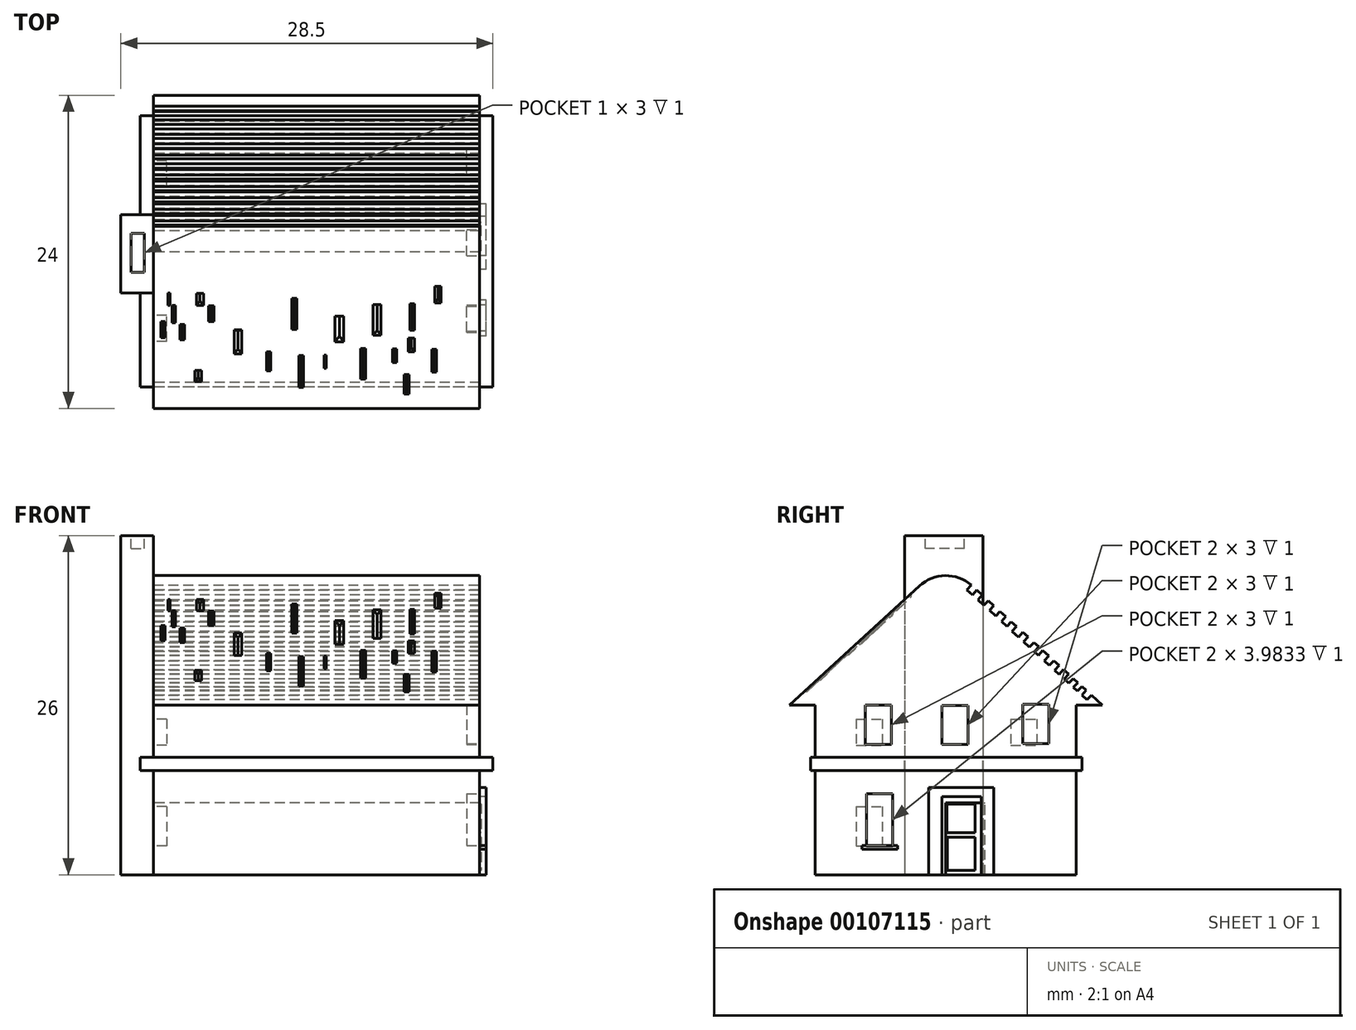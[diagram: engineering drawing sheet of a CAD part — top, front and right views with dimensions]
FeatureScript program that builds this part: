
annotation { "Feature Type Name" : "Feature", "Feature Type Description" : "" }
export const myFeature = defineFeature(function(context is Context, id is Id, definition is map)
    precondition{}
    {
        {
            var Q0;
            Q0=qCreatedBy(makeId("Right.planeOp"),FACE);
            var sketch = newSketch(context, id + "F0", { "sketchPlane" : qUnion([Q0])});
            skLineSegment(sketch, "E0.bottom", {"start": v(0, 0) * mm, "end": v(20, 0) * mm});
            skLineSegment(sketch, "E0.top", {"start": v(0, 13) * mm, "end": v(20, 13) * mm});
            skLineSegment(sketch, "E0.left", {"start": v(0, 0) * mm, "end": v(0, 13) * mm});
            skLineSegment(sketch, "E0.right", {"start": v(20, 0) * mm, "end": v(20, 13) * mm});
            skLineSegment(sketch, "E1", {"start": v(10, 13) * mm, "end": v(10, 24) * mm, "construction": true});
            skLineSegment(sketch, "E2", {"start": v(0, 13) * mm, "end": v(-2, 13) * mm});
            skLineSegment(sketch, "E3", {"start": v(20, 13) * mm, "end": v(22, 13) * mm});
            skLineSegment(sketch, "E4", {"start": v(-2, 13) * mm, "end": v(10, 24) * mm});
            skLineSegment(sketch, "E5", {"start": v(22, 13) * mm, "end": v(10, 24) * mm});
            skLineSegment(sketch, "E6.bottom", {"start": v(10, 0) * mm, "end": v(13, 0) * mm});
            skLineSegment(sketch, "E6.top", {"start": v(10, 5.5) * mm, "end": v(13, 5.5) * mm});
            skLineSegment(sketch, "E6.left", {"start": v(10, 0) * mm, "end": v(10, 5.5) * mm});
            skLineSegment(sketch, "E6.right", {"start": v(13, 0) * mm, "end": v(13, 5.5) * mm});
            skLineSegment(sketch, "E7.bottom", {"start": v(3.14, 5.21) * mm, "end": v(5.14, 5.21) * mm});
            skLineSegment(sketch, "E7.top", {"start": v(3.14, 2.21) * mm, "end": v(5.14, 2.21) * mm});
            skLineSegment(sketch, "E7.left", {"start": v(3.14, 5.21) * mm, "end": v(3.14, 2.21) * mm});
            skLineSegment(sketch, "E7.right", {"start": v(5.14, 5.21) * mm, "end": v(5.14, 2.21) * mm});
            skLineSegment(sketch, "E8.bottom", {"start": v(3.14, 11.94) * mm, "end": v(5.14, 11.94) * mm});
            skLineSegment(sketch, "E8.top", {"start": v(3.14, 9.94) * mm, "end": v(5.14, 9.94) * mm});
            skLineSegment(sketch, "E8.left", {"start": v(3.14, 11.94) * mm, "end": v(3.14, 9.94) * mm});
            skLineSegment(sketch, "E8.right", {"start": v(5.14, 11.94) * mm, "end": v(5.14, 9.94) * mm});
            skLineSegment(sketch, "E9.bottom", {"start": v(8.85, 11.94) * mm, "end": v(10.85, 11.94) * mm});
            skLineSegment(sketch, "E9.top", {"start": v(8.85, 9.94) * mm, "end": v(10.85, 9.94) * mm});
            skLineSegment(sketch, "E9.left", {"start": v(8.85, 11.94) * mm, "end": v(8.85, 9.94) * mm});
            skLineSegment(sketch, "E9.right", {"start": v(10.85, 11.94) * mm, "end": v(10.85, 9.94) * mm});
            skLineSegment(sketch, "E10.bottom", {"start": v(14.97, 11.94) * mm, "end": v(16.97, 11.94) * mm});
            skLineSegment(sketch, "E10.top", {"start": v(14.97, 9.94) * mm, "end": v(16.97, 9.94) * mm});
            skLineSegment(sketch, "E10.left", {"start": v(14.97, 11.94) * mm, "end": v(14.97, 9.94) * mm});
            skLineSegment(sketch, "E10.right", {"start": v(16.97, 11.94) * mm, "end": v(16.97, 9.94) * mm});
            skSolve(sketch);
        }
        {
            var Q0;
            Q0=makeQuery(id+"F0.imprint","IMPRINT",FACE,{"disambiguationData":[TD([[makeQuery(id+"F0.imprint","IMPRINT",EDGE,{"derivedFrom":sQuery(id+"F0.wireOp",EDGE,"E0.top")}),1.0]])]});
            var Q1;
            Q1=makeQuery(id+"F0.imprint","IMPRINT",FACE,{"disambiguationData":[TD([[makeQuery(id+"F0.imprint","IMPRINT",EDGE,{"derivedFrom":sQuery(id+"F0.wireOp",EDGE,"E8.bottom")}),-1.0]])]});
            var Q2;
            Q2=makeQuery(id+"F0.imprint","IMPRINT",FACE,{"disambiguationData":[TD([[makeQuery(id+"F0.imprint","IMPRINT",EDGE,{"derivedFrom":sQuery(id+"F0.wireOp",EDGE,"E9.bottom")}),-1.0]])]});
            var Q3;
            Q3=makeQuery(id+"F0.imprint","IMPRINT",FACE,{"disambiguationData":[TD([[makeQuery(id+"F0.imprint","IMPRINT",EDGE,{"derivedFrom":sQuery(id+"F0.wireOp",EDGE,"E10.bottom")}),-1.0]])]});
            var Q4;
            Q4=makeQuery(id+"F0.imprint","IMPRINT",FACE,{"disambiguationData":[TD([[makeQuery(id+"F0.imprint","IMPRINT",EDGE,{"derivedFrom":sQuery(id+"F0.wireOp",EDGE,"E6.bottom")}),1.0]])]});
            var Q5;
            Q5=makeQuery(id+"F0.imprint","IMPRINT",FACE,{"disambiguationData":[TD([[makeQuery(id+"F0.imprint","IMPRINT",EDGE,{"derivedFrom":sQuery(id+"F0.wireOp",EDGE,"E7.bottom")}),-1.0]])]});
            var Q6;
            Q6=makeQuery(id+"F0.imprint","IMPRINT",FACE,{"disambiguationData":[TD([[makeQuery(id+"F0.imprint","IMPRINT",EDGE,{"derivedFrom":sQuery(id+"F0.wireOp",EDGE,"E0.top")}),-1.0]])]});
            extrude(context, id + "F1", {"entities" : qUnion([Q0, Q1, Q2, Q3, Q4, Q5, Q6]), "depth" : 25 * mm});
        }
        {
            var Q0;
            Q0=makeQuery(id+"F0.imprint","IMPRINT",FACE,{"disambiguationData":[TD([[makeQuery(id+"F0.imprint","IMPRINT",EDGE,{"derivedFrom":sQuery(id+"F0.wireOp",EDGE,"E10.bottom")}),-1.0]])]});
            var Q1;
            Q1=makeQuery(id+"F0.imprint","IMPRINT",FACE,{"disambiguationData":[TD([[makeQuery(id+"F0.imprint","IMPRINT",EDGE,{"derivedFrom":sQuery(id+"F0.wireOp",EDGE,"E8.bottom")}),-1.0]])]});
            var Q2;
            Q2=makeQuery(id+"F0.imprint","IMPRINT",FACE,{"disambiguationData":[TD([[makeQuery(id+"F0.imprint","IMPRINT",EDGE,{"derivedFrom":sQuery(id+"F0.wireOp",EDGE,"E7.bottom")}),-1.0]])]});
            extrude(context, id + "F2", {"entities" : qUnion([Q0, Q1, Q2]), "operationType" : NewBodyOperationType.REMOVE, "depth" : 1 * mm});
        }
        {
            var Q0;
            Q0=makeQuery(id+"F1.opExtrude","CAP_FACE",FACE,{"disambiguationData":[OSD([sQuery(id+"F0.wireOp",EDGE,"E0.bottom"),sQuery(id+"F0.wireOp",EDGE,"E0.left"),sQuery(id+"F0.wireOp",EDGE,"E0.right"),sQuery(id+"F0.wireOp",EDGE,"E2"),sQuery(id+"F0.wireOp",EDGE,"E3"),sQuery(id+"F0.wireOp",EDGE,"E4"),sQuery(id+"F0.wireOp",EDGE,"E5"),sQuery(id+"F0.wireOp",EDGE,"E6.bottom")])],"isStart":false});
            cPlane(context, id + "F3", {"entities" : qUnion([Q0]), "cplaneType" : CPlaneType.OFFSET, "offset" : 0 * mm, "width" : 150 * mm, "height" : 150 * mm});
        }
        {
            var Q0;
            Q0=qCreatedBy(id+"F3.planeOp",FACE);
            var sketch = newSketch(context, id + "F4", { "sketchPlane" : qUnion([Q0])});
            skLineSegment(sketch, "E11.bottom", {"start": v(3.83, 13) * mm, "end": v(5.83, 13) * mm});
            skLineSegment(sketch, "E11.top", {"start": v(3.83, 10) * mm, "end": v(5.83, 10) * mm});
            skLineSegment(sketch, "E11.left", {"start": v(3.83, 13) * mm, "end": v(3.83, 10) * mm});
            skLineSegment(sketch, "E11.right", {"start": v(5.83, 13) * mm, "end": v(5.83, 10) * mm});
            skLineSegment(sketch, "E12.bottom", {"start": v(9.7, 12.98) * mm, "end": v(11.7, 12.98) * mm});
            skLineSegment(sketch, "E12.top", {"start": v(9.7, 9.98) * mm, "end": v(11.7, 9.98) * mm});
            skLineSegment(sketch, "E12.left", {"start": v(9.7, 12.98) * mm, "end": v(9.7, 9.98) * mm});
            skLineSegment(sketch, "E12.right", {"start": v(11.7, 12.98) * mm, "end": v(11.7, 9.98) * mm});
            skLineSegment(sketch, "E13.bottom", {"start": v(15.88, 13.05) * mm, "end": v(17.88, 13.05) * mm});
            skLineSegment(sketch, "E13.top", {"start": v(15.88, 10.05) * mm, "end": v(17.88, 10.05) * mm});
            skLineSegment(sketch, "E13.left", {"start": v(15.88, 13.05) * mm, "end": v(15.88, 10.05) * mm});
            skLineSegment(sketch, "E13.right", {"start": v(17.88, 13.05) * mm, "end": v(17.88, 10.05) * mm});
            skLineSegment(sketch, "E14.bottom", {"start": v(3.92, 6.22) * mm, "end": v(5.92, 6.22) * mm});
            skLineSegment(sketch, "E14.top", {"start": v(3.92, 2.22) * mm, "end": v(5.92, 2.22) * mm});
            skLineSegment(sketch, "E14.left", {"start": v(3.92, 6.22) * mm, "end": v(3.92, 2.22) * mm});
            skLineSegment(sketch, "E14.right", {"start": v(5.92, 6.22) * mm, "end": v(5.92, 2.22) * mm});
            skLineSegment(sketch, "E15.bottom", {"start": v(9.72, 6) * mm, "end": v(12.72, 6) * mm});
            skLineSegment(sketch, "E15.top", {"start": v(9.72, 0) * mm, "end": v(12.72, 0) * mm});
            skLineSegment(sketch, "E15.left", {"start": v(9.72, 6) * mm, "end": v(9.72, 0) * mm});
            skLineSegment(sketch, "E15.right", {"start": v(12.72, 6) * mm, "end": v(12.72, 0) * mm});
            skLineSegment(sketch, "E16.bottom", {"start": v(8.67, 6.7) * mm, "end": v(13.67, 6.7) * mm});
            skLineSegment(sketch, "E16.top", {"start": v(8.67, 0) * mm, "end": v(13.67, 0) * mm});
            skLineSegment(sketch, "E16.left", {"start": v(8.67, 6.7) * mm, "end": v(8.67, 0) * mm});
            skLineSegment(sketch, "E16.right", {"start": v(13.67, 6.7) * mm, "end": v(13.67, 0) * mm});
            skLineSegment(sketch, "E17.bottom", {"start": v(10.09, 5.42) * mm, "end": v(12.24, 5.42) * mm});
            skLineSegment(sketch, "E17.top", {"start": v(10.09, 3.23) * mm, "end": v(12.24, 3.23) * mm});
            skLineSegment(sketch, "E17.left", {"start": v(10.09, 5.42) * mm, "end": v(10.09, 3.23) * mm});
            skLineSegment(sketch, "E17.right", {"start": v(12.24, 5.42) * mm, "end": v(12.24, 3.23) * mm});
            skLineSegment(sketch, "E18.bottom", {"start": v(10.13, 2.87) * mm, "end": v(12.24, 2.87) * mm});
            skLineSegment(sketch, "E18.top", {"start": v(10.13, 0.32) * mm, "end": v(12.24, 0.32) * mm});
            skLineSegment(sketch, "E18.left", {"start": v(10.13, 2.87) * mm, "end": v(10.13, 0.32) * mm});
            skLineSegment(sketch, "E18.right", {"start": v(12.24, 2.87) * mm, "end": v(12.24, 0.32) * mm});
            skLineSegment(sketch, "E19.bottom", {"start": v(3.56, 2.23) * mm, "end": v(6.3, 2.23) * mm});
            skLineSegment(sketch, "E19.top", {"start": v(3.56, 1.94) * mm, "end": v(6.3, 1.94) * mm});
            skLineSegment(sketch, "E19.left", {"start": v(3.56, 2.23) * mm, "end": v(3.56, 1.94) * mm});
            skLineSegment(sketch, "E19.right", {"start": v(6.3, 2.23) * mm, "end": v(6.3, 1.94) * mm});
            skLineSegment(sketch, "E20", {"start": v(0, 9) * mm, "end": v(20.43, 9) * mm});
            skLineSegment(sketch, "E21", {"start": v(20.43, 9) * mm, "end": v(20.43, 8) * mm});
            skLineSegment(sketch, "E22", {"start": v(20.43, 8) * mm, "end": v(-0.36, 8) * mm});
            skLineSegment(sketch, "E23", {"start": v(-0.36, 8) * mm, "end": v(-0.36, 9) * mm});
            skLineSegment(sketch, "E24", {"start": v(-0.36, 9) * mm, "end": v(0, 9) * mm});
            skSolve(sketch);
        }
        {
            var Q0;
            {var subQ5=sQuery(id+"F4.wireOp",EDGE,"E14.top");Q0=makeQuery(id+"F4.imprint","IMPRINT",FACE,{"disambiguationData":[TD([[makeQuery(id+"F4.imprint","IMPRINT",EDGE,{"derivedFrom":subQ5}),-1.0]])]});}
            var Q1;
            Q1=makeQuery(id+"F4.imprint","IMPRINT",FACE,{"disambiguationData":[TD([[makeQuery(id+"F4.imprint","IMPRINT",EDGE,{"derivedFrom":sQuery(id+"F4.wireOp",EDGE,"E15.bottom")}),1.0]])]});
            extrude(context, id + "F5", {"entities" : qUnion([Q0, Q1]), "operationType" : NewBodyOperationType.ADD, "depth" : .5 * mm});
        }
        {
            var Q0;
            {var subQ0=sQuery(id+"F4.wireOp",EDGE,"E14.bottom");Q0=makeQuery(id+"F4.imprint","IMPRINT",FACE,{"disambiguationData":[TD([[makeQuery(id+"F4.imprint","IMPRINT",EDGE,{"derivedFrom":subQ0}),-1.0]])]});}
            var Q1;
            Q1=makeQuery(id+"F4.imprint","IMPRINT",FACE,{"disambiguationData":[TD([[makeQuery(id+"F4.imprint","IMPRINT",EDGE,{"derivedFrom":sQuery(id+"F4.wireOp",EDGE,"E11.bottom")}),-1.0]])]});
            var Q2;
            Q2=makeQuery(id+"F4.imprint","IMPRINT",FACE,{"disambiguationData":[TD([[makeQuery(id+"F4.imprint","IMPRINT",EDGE,{"derivedFrom":sQuery(id+"F4.wireOp",EDGE,"E12.bottom")}),-1.0]])]});
            var Q3;
            Q3=makeQuery(id+"F4.imprint","IMPRINT",FACE,{"disambiguationData":[TD([[makeQuery(id+"F4.imprint","IMPRINT",EDGE,{"derivedFrom":sQuery(id+"F4.wireOp",EDGE,"E13.bottom")}),-1.0]])]});
            extrude(context, id + "F6", {"entities" : qUnion([Q0, Q1, Q2, Q3]), "operationType" : NewBodyOperationType.REMOVE, "oppositeDirection" : true, "depth" : 1 * mm});
        }
        {
            var Q0;
            Q0=makeQuery(id+"F4.imprint","IMPRINT",FACE,{"disambiguationData":[TD([[makeQuery(id+"F4.imprint","IMPRINT",EDGE,{"derivedFrom":sQuery(id+"F4.wireOp",EDGE,"E17.bottom")}),-1.0]])]});
            var Q1;
            Q1=makeQuery(id+"F4.imprint","IMPRINT",FACE,{"disambiguationData":[TD([[makeQuery(id+"F4.imprint","IMPRINT",EDGE,{"derivedFrom":sQuery(id+"F4.wireOp",EDGE,"E18.bottom")}),-1.0]])]});
            extrude(context, id + "F7", {"entities" : qUnion([Q0, Q1]), "operationType" : NewBodyOperationType.ADD, "depth" : .1 * mm});
        }
        {
            var Q0;
            Q0=qCreatedBy(makeId("Top.planeOp"),FACE);
            var sketch = newSketch(context, id + "F8", { "sketchPlane" : qUnion([Q0])});
            skLineSegment(sketch, "E25.bottom", {"start": v(0, 12.85) * mm, "end": v(-2.5, 12.85) * mm});
            skLineSegment(sketch, "E25.top", {"start": v(0, 6.85) * mm, "end": v(-2.5, 6.85) * mm});
            skLineSegment(sketch, "E25.left", {"start": v(0, 12.85) * mm, "end": v(0, 6.85) * mm});
            skLineSegment(sketch, "E25.right", {"start": v(-2.5, 12.85) * mm, "end": v(-2.5, 6.85) * mm});
            skSolve(sketch);
        }
        {
            var Q0;
            Q0=makeQuery(id+"F8.imprint","IMPRINT",FACE,{"disambiguationData":[TD([[makeQuery(id+"F8.imprint","IMPRINT",EDGE,{"derivedFrom":sQuery(id+"F8.wireOp",EDGE,"E25.bottom")}),1.0]])]});
            extrude(context, id + "F9", {"entities" : qUnion([Q0]), "operationType" : NewBodyOperationType.ADD, "depth" : 26 * mm});
        }
        {
            var Q0;
            Q0=makeQuery(id+"F9.opExtrude","CAP_FACE",FACE,{"disambiguationData":[OSD([sQuery(id+"F8.wireOp",EDGE,"E25.bottom"),sQuery(id+"F8.wireOp",EDGE,"E25.top"),sQuery(id+"F8.wireOp",EDGE,"E25.left"),sQuery(id+"F8.wireOp",EDGE,"E25.right")])],"isStart":false});
            cPlane(context, id + "F10", {"entities" : qUnion([Q0]), "cplaneType" : CPlaneType.OFFSET, "offset" : 0 * mm, "width" : 150 * mm, "height" : 150 * mm});
        }
        {
            var Q0;
            Q0=qCreatedBy(id+"F10.planeOp",FACE);
            var sketch = newSketch(context, id + "F11", { "sketchPlane" : qUnion([Q0])});
            skLineSegment(sketch, "E26.bottom", {"start": v(-1.7, 11.43) * mm, "end": v(-0.7, 11.43) * mm});
            skLineSegment(sketch, "E26.top", {"start": v(-1.7, 8.43) * mm, "end": v(-0.7, 8.43) * mm});
            skLineSegment(sketch, "E26.left", {"start": v(-1.7, 11.43) * mm, "end": v(-1.7, 8.43) * mm});
            skLineSegment(sketch, "E26.right", {"start": v(-0.7, 11.43) * mm, "end": v(-0.7, 8.43) * mm});
            skSolve(sketch);
        }
        {
            var Q0;
            Q0 = qSketchRegion(id + "F11", true);
            extrude(context, id + "F12", {"entities" : qUnion([Q0]), "operationType" : NewBodyOperationType.REMOVE, "oppositeDirection" : true, "depth" : 1 * mm});
        }
        {
            var Q0;
            Q0=makeQuery(id+"F1.opExtrude","SWEPT_EDGE",EDGE,{"disambiguationData":[OSD([sQuery(id+"F0.wireOp",EDGE,"E4"),sQuery(id+"F0.wireOp",EDGE,"E5")])]});
            fillet(context, id + "F13", {"entities" : qUnion([Q0]), "radius" : 3 * mm, "tangentPropagation" : true, "allowEdgeOverflow" : false});
        }
        {
            var Q0;
            Q0=makeQuery(id+"F4.imprint","IMPRINT",FACE,{"disambiguationData":[TD([[makeQuery(id+"F4.imprint","IMPRINT",EDGE,{"derivedFrom":sQuery(id+"F4.wireOp",EDGE,"E20")}),-1.0]])]});
            extrude(context, id + "F14", {"entities" : qUnion([Q0]), "operationType" : NewBodyOperationType.ADD, "depth" : 1 * mm, "hasSecondDirection" : true, "secondDirectionOppositeDirection" : true, "secondDirectionDepth" : 26 * mm});
        }
        {
            var Q0;
            Q0=makeQuery(id+"F1.opExtrude","SWEPT_FACE",FACE,{"disambiguationData":[OSD([sQuery(id+"F0.wireOp",EDGE,"E4")])]});
            var sketch = newSketch(context, id + "F15", { "sketchPlane" : qUnion([Q0])});
            skLineSegment(sketch, "E27.bottom", {"start": v(1.1, 19.31) * mm, "end": v(1.27, 19.31) * mm});
            skLineSegment(sketch, "E27.left", {"start": v(1.1, 19.31) * mm, "end": v(1.1, 18.01) * mm});
            skLineSegment(sketch, "E28.bottom", {"start": v(1.42, 18.01) * mm, "end": v(1.68, 18.01) * mm});
            skLineSegment(sketch, "E28.top", {"start": v(1.42, 16.2) * mm, "end": v(1.68, 16.2) * mm});
            skLineSegment(sketch, "E28.left", {"start": v(1.42, 18.01) * mm, "end": v(1.42, 16.2) * mm});
            skLineSegment(sketch, "E28.right", {"start": v(1.68, 18.01) * mm, "end": v(1.68, 16.2) * mm});
            skLineSegment(sketch, "E29.bottom", {"start": v(2.04, 16.05) * mm, "end": v(2.39, 16.05) * mm});
            skLineSegment(sketch, "E29.top", {"start": v(2.04, 14.43) * mm, "end": v(2.39, 14.43) * mm});
            skLineSegment(sketch, "E29.left", {"start": v(2.04, 16.05) * mm, "end": v(2.04, 14.43) * mm});
            skLineSegment(sketch, "E29.right", {"start": v(2.39, 16.05) * mm, "end": v(2.39, 14.43) * mm});
            skLineSegment(sketch, "E30.bottom", {"start": v(0.56, 16.32) * mm, "end": v(0.87, 16.32) * mm});
            skLineSegment(sketch, "E30.top", {"start": v(0.56, 14.66) * mm, "end": v(0.87, 14.66) * mm});
            skLineSegment(sketch, "E30.left", {"start": v(0.56, 16.32) * mm, "end": v(0.56, 14.66) * mm});
            skLineSegment(sketch, "E30.right", {"start": v(0.87, 16.32) * mm, "end": v(0.87, 14.66) * mm});
            skLineSegment(sketch, "E31.bottom", {"start": v(4.23, 17.97) * mm, "end": v(4.63, 17.97) * mm});
            skLineSegment(sketch, "E31.top", {"start": v(4.23, 16.36) * mm, "end": v(4.63, 16.36) * mm});
            skLineSegment(sketch, "E31.left", {"start": v(4.23, 17.97) * mm, "end": v(4.23, 16.36) * mm});
            skLineSegment(sketch, "E31.right", {"start": v(4.63, 17.97) * mm, "end": v(4.63, 16.36) * mm});
            skLineSegment(sketch, "E32.bottom", {"start": v(3.3, 19.29) * mm, "end": v(3.83, 19.29) * mm});
            skLineSegment(sketch, "E32.top", {"start": v(3.3, 18.02) * mm, "end": v(3.83, 18.02) * mm});
            skLineSegment(sketch, "E32.left", {"start": v(3.3, 19.29) * mm, "end": v(3.3, 18.02) * mm});
            skLineSegment(sketch, "E32.right", {"start": v(3.83, 19.29) * mm, "end": v(3.83, 18.02) * mm});
            skLineSegment(sketch, "E33.bottom", {"start": v(6.19, 15.48) * mm, "end": v(6.78, 15.48) * mm});
            skLineSegment(sketch, "E33.top", {"start": v(6.19, 12.96) * mm, "end": v(6.78, 12.96) * mm});
            skLineSegment(sketch, "E33.left", {"start": v(6.19, 15.48) * mm, "end": v(6.19, 12.96) * mm});
            skLineSegment(sketch, "E33.right", {"start": v(6.78, 15.48) * mm, "end": v(6.78, 12.96) * mm});
            skLineSegment(sketch, "E34.bottom", {"start": v(11, 18.77) * mm, "end": v(10.62, 18.77) * mm});
            skLineSegment(sketch, "E34.top", {"start": v(11, 15.51) * mm, "end": v(10.62, 15.51) * mm});
            skLineSegment(sketch, "E34.left", {"start": v(11, 18.77) * mm, "end": v(11, 15.51) * mm});
            skLineSegment(sketch, "E34.right", {"start": v(10.62, 18.77) * mm, "end": v(10.62, 15.51) * mm});
            skLineSegment(sketch, "E35.bottom", {"start": v(9, 13.18) * mm, "end": v(8.65, 13.18) * mm});
            skLineSegment(sketch, "E35.top", {"start": v(9, 11.23) * mm, "end": v(8.65, 11.23) * mm});
            skLineSegment(sketch, "E35.left", {"start": v(9, 13.18) * mm, "end": v(9, 11.23) * mm});
            skLineSegment(sketch, "E35.right", {"start": v(8.65, 13.18) * mm, "end": v(8.65, 11.23) * mm});
            skLineSegment(sketch, "E36.bottom", {"start": v(13.91, 16.92) * mm, "end": v(14.57, 16.92) * mm});
            skLineSegment(sketch, "E36.top", {"start": v(13.91, 14.25) * mm, "end": v(14.57, 14.25) * mm});
            skLineSegment(sketch, "E36.left", {"start": v(13.91, 16.92) * mm, "end": v(13.91, 14.25) * mm});
            skLineSegment(sketch, "E36.right", {"start": v(14.57, 16.92) * mm, "end": v(14.57, 14.25) * mm});
            skLineSegment(sketch, "E37.bottom", {"start": v(11.15, 12.8) * mm, "end": v(11.5, 12.8) * mm});
            skLineSegment(sketch, "E37.top", {"start": v(11.15, 9.48) * mm, "end": v(11.5, 9.48) * mm});
            skLineSegment(sketch, "E37.left", {"start": v(11.15, 12.8) * mm, "end": v(11.15, 9.48) * mm});
            skLineSegment(sketch, "E37.right", {"start": v(11.5, 12.8) * mm, "end": v(11.5, 9.48) * mm});
            skLineSegment(sketch, "E38.bottom", {"start": v(16.84, 18.13) * mm, "end": v(17.42, 18.13) * mm});
            skLineSegment(sketch, "E38.top", {"start": v(16.84, 14.9) * mm, "end": v(17.42, 14.9) * mm});
            skLineSegment(sketch, "E38.left", {"start": v(16.84, 18.13) * mm, "end": v(16.84, 14.9) * mm});
            skLineSegment(sketch, "E38.right", {"start": v(17.42, 18.13) * mm, "end": v(17.42, 14.9) * mm});
            skLineSegment(sketch, "E39.bottom", {"start": v(15.86, 13.53) * mm, "end": v(16.25, 13.53) * mm});
            skLineSegment(sketch, "E39.top", {"start": v(15.86, 10.36) * mm, "end": v(16.25, 10.36) * mm});
            skLineSegment(sketch, "E39.left", {"start": v(15.86, 13.53) * mm, "end": v(15.86, 10.36) * mm});
            skLineSegment(sketch, "E39.right", {"start": v(16.25, 13.53) * mm, "end": v(16.25, 10.36) * mm});
            skLineSegment(sketch, "E40.bottom", {"start": v(13.09, 12.87) * mm, "end": v(13.25, 12.87) * mm});
            skLineSegment(sketch, "E40.top", {"start": v(13.09, 11.46) * mm, "end": v(13.25, 11.46) * mm});
            skLineSegment(sketch, "E40.left", {"start": v(13.09, 12.87) * mm, "end": v(13.09, 11.46) * mm});
            skLineSegment(sketch, "E40.right", {"start": v(13.25, 12.87) * mm, "end": v(13.25, 11.46) * mm});
            skLineSegment(sketch, "E41.bottom", {"start": v(19.66, 18.18) * mm, "end": v(19.99, 18.18) * mm});
            skLineSegment(sketch, "E41.top", {"start": v(19.66, 15.42) * mm, "end": v(19.99, 15.42) * mm});
            skLineSegment(sketch, "E41.left", {"start": v(19.66, 18.18) * mm, "end": v(19.66, 15.42) * mm});
            skLineSegment(sketch, "E41.right", {"start": v(19.99, 18.18) * mm, "end": v(19.99, 15.42) * mm});
            skLineSegment(sketch, "E42.bottom", {"start": v(19.54, 14.62) * mm, "end": v(19.99, 14.62) * mm});
            skLineSegment(sketch, "E42.top", {"start": v(19.54, 13.21) * mm, "end": v(19.99, 13.21) * mm});
            skLineSegment(sketch, "E42.left", {"start": v(19.54, 14.62) * mm, "end": v(19.54, 13.21) * mm});
            skLineSegment(sketch, "E42.right", {"start": v(19.99, 14.62) * mm, "end": v(19.99, 13.21) * mm});
            skLineSegment(sketch, "E43.bottom", {"start": v(18.31, 13.49) * mm, "end": v(18.64, 13.49) * mm});
            skLineSegment(sketch, "E43.top", {"start": v(18.31, 12.08) * mm, "end": v(18.64, 12.08) * mm});
            skLineSegment(sketch, "E43.left", {"start": v(18.31, 13.49) * mm, "end": v(18.31, 12.08) * mm});
            skLineSegment(sketch, "E43.right", {"start": v(18.64, 13.49) * mm, "end": v(18.64, 12.08) * mm});
            skLineSegment(sketch, "E44.bottom", {"start": v(21.57, 20) * mm, "end": v(22.04, 20) * mm});
            skLineSegment(sketch, "E44.top", {"start": v(21.57, 18.3) * mm, "end": v(22.04, 18.3) * mm});
            skLineSegment(sketch, "E44.left", {"start": v(21.57, 20) * mm, "end": v(21.57, 18.3) * mm});
            skLineSegment(sketch, "E44.right", {"start": v(22.04, 20) * mm, "end": v(22.04, 18.3) * mm});
            skLineSegment(sketch, "E45.bottom", {"start": v(21.33, 13.44) * mm, "end": v(21.68, 13.44) * mm});
            skLineSegment(sketch, "E45.top", {"start": v(21.33, 11.08) * mm, "end": v(21.68, 11.08) * mm});
            skLineSegment(sketch, "E45.left", {"start": v(21.33, 13.44) * mm, "end": v(21.33, 11.08) * mm});
            skLineSegment(sketch, "E45.right", {"start": v(21.68, 13.44) * mm, "end": v(21.68, 11.08) * mm});
            skLineSegment(sketch, "E46.bottom", {"start": v(19.21, 10.82) * mm, "end": v(19.58, 10.82) * mm});
            skLineSegment(sketch, "E46.top", {"start": v(19.21, 8.8) * mm, "end": v(19.58, 8.8) * mm});
            skLineSegment(sketch, "E46.left", {"start": v(19.21, 10.82) * mm, "end": v(19.21, 8.8) * mm});
            skLineSegment(sketch, "E46.right", {"start": v(19.58, 10.82) * mm, "end": v(19.58, 8.8) * mm});
            skLineSegment(sketch, "E47.bottom", {"start": v(3.18, 11.26) * mm, "end": v(3.68, 11.26) * mm});
            skLineSegment(sketch, "E47.top", {"start": v(3.18, 10.1) * mm, "end": v(3.68, 10.1) * mm});
            skLineSegment(sketch, "E47.left", {"start": v(3.18, 11.26) * mm, "end": v(3.18, 10.1) * mm});
            skLineSegment(sketch, "E47.right", {"start": v(3.68, 11.26) * mm, "end": v(3.68, 10.1) * mm});
            skLineSegment(sketch, "E48", {"start": v(1.1, 18.01) * mm, "end": v(1.27, 18.01) * mm});
            skLineSegment(sketch, "E49", {"start": v(1.27, 18.01) * mm, "end": v(1.27, 19.31) * mm});
            skSolve(sketch);
        }
        {
            var Q0;
            Q0 = qSketchRegion(id + "F15", true);
            extrude(context, id + "F16", {"entities" : qUnion([Q0]), "operationType" : NewBodyOperationType.REMOVE, "oppositeDirection" : true, "depth" : .5 * mm, "hasDraft" : true, "draftAngle" : 50 * degree, "draftPullDirection" : true});
        }
        {
            var Q0;
            Q0=qCreatedBy(makeId("Right.planeOp"),FACE);
            var sketch = newSketch(context, id + "F17", { "sketchPlane" : qUnion([Q0])});
            skLineSegment(sketch, "E50", {"start": v(12.3, 22.57) * mm, "end": v(21.88, 13.79) * mm});
            skLineSegment(sketch, "E51", {"start": v(21.88, 13.79) * mm, "end": v(21.2, 13.05) * mm});
            skLineSegment(sketch, "E52", {"start": v(20.82, 13.4) * mm, "end": v(20.42, 13.77) * mm});
            skLineSegment(sketch, "E53", {"start": v(11.62, 21.84) * mm, "end": v(12.3, 22.57) * mm});
            skLineSegment(sketch, "E54", {"start": v(12.71, 22.2) * mm, "end": v(12.04, 21.45) * mm});
            skLineSegment(sketch, "E55", {"start": v(12.45, 21.07) * mm, "end": v(13.13, 21.81) * mm});
            skLineSegment(sketch, "E56", {"start": v(13.13, 21.81) * mm, "end": v(13.6, 21.39) * mm});
            skLineSegment(sketch, "E57", {"start": v(13.6, 21.39) * mm, "end": v(12.92, 20.65) * mm});
            skLineSegment(sketch, "E58", {"start": v(13.34, 20.26) * mm, "end": v(14.01, 21) * mm});
            skLineSegment(sketch, "E59", {"start": v(14.01, 21) * mm, "end": v(14.5, 20.55) * mm});
            skLineSegment(sketch, "E60", {"start": v(14.5, 20.55) * mm, "end": v(13.82, 19.82) * mm});
            skLineSegment(sketch, "E61", {"start": v(14.26, 19.42) * mm, "end": v(14.93, 20.16) * mm});
            skLineSegment(sketch, "E62", {"start": v(14.93, 20.16) * mm, "end": v(15.35, 19.77) * mm});
            skLineSegment(sketch, "E63", {"start": v(15.35, 19.77) * mm, "end": v(14.68, 19.03) * mm});
            skLineSegment(sketch, "E64", {"start": v(15.08, 18.67) * mm, "end": v(15.75, 19.4) * mm});
            skLineSegment(sketch, "E65", {"start": v(15.75, 19.4) * mm, "end": v(16.24, 18.96) * mm});
            skLineSegment(sketch, "E66", {"start": v(16.24, 18.96) * mm, "end": v(15.56, 18.22) * mm});
            skLineSegment(sketch, "E67", {"start": v(15.96, 17.86) * mm, "end": v(16.63, 18.6) * mm});
            skLineSegment(sketch, "E68", {"start": v(16.63, 18.6) * mm, "end": v(17.09, 18.18) * mm});
            skLineSegment(sketch, "E69", {"start": v(17.09, 18.18) * mm, "end": v(16.41, 17.44) * mm});
            skLineSegment(sketch, "E70", {"start": v(16.79, 17.1) * mm, "end": v(17.46, 17.84) * mm});
            skLineSegment(sketch, "E71", {"start": v(17.46, 17.84) * mm, "end": v(17.77, 17.56) * mm});
            skLineSegment(sketch, "E72", {"start": v(17.77, 17.56) * mm, "end": v(17.1, 16.82) * mm});
            skLineSegment(sketch, "E73", {"start": v(17.55, 16.4) * mm, "end": v(18.23, 17.14) * mm});
            skLineSegment(sketch, "E74", {"start": v(18.23, 17.14) * mm, "end": v(18.61, 16.78) * mm});
            skLineSegment(sketch, "E75", {"start": v(18.61, 16.78) * mm, "end": v(17.94, 16.05) * mm});
            skLineSegment(sketch, "E76", {"start": v(18.34, 15.68) * mm, "end": v(19.01, 16.42) * mm});
            skLineSegment(sketch, "E77", {"start": v(19.01, 16.42) * mm, "end": v(19.35, 16.1) * mm});
            skLineSegment(sketch, "E78", {"start": v(19.35, 16.1) * mm, "end": v(18.68, 15.37) * mm});
            skLineSegment(sketch, "E79", {"start": v(19.07, 15) * mm, "end": v(19.75, 15.74) * mm});
            skLineSegment(sketch, "E80", {"start": v(19.75, 15.74) * mm, "end": v(20.1, 15.42) * mm});
            skLineSegment(sketch, "E81", {"start": v(20.1, 15.42) * mm, "end": v(19.43, 14.68) * mm});
            skLineSegment(sketch, "E82", {"start": v(19.77, 14.37) * mm, "end": v(20.45, 15.1) * mm});
            skLineSegment(sketch, "E83", {"start": v(20.45, 15.1) * mm, "end": v(20.76, 14.81) * mm});
            skLineSegment(sketch, "E84", {"start": v(20.76, 14.81) * mm, "end": v(20.09, 14.08) * mm});
            skLineSegment(sketch, "E85", {"start": v(20.42, 13.77) * mm, "end": v(21.1, 14.5) * mm});
            skLineSegment(sketch, "E86", {"start": v(21.1, 14.5) * mm, "end": v(21.5, 14.14) * mm});
            skLineSegment(sketch, "E87", {"start": v(21.5, 14.14) * mm, "end": v(20.82, 13.4) * mm});
            skLineSegment(sketch, "E88.trimOffspring", {"start": v(12.04, 21.45) * mm, "end": v(11.62, 21.84) * mm});
            skLineSegment(sketch, "E89.trimOffspring", {"start": v(12.92, 20.65) * mm, "end": v(12.45, 21.07) * mm});
            skLineSegment(sketch, "E90.trimOffspring", {"start": v(13.82, 19.82) * mm, "end": v(13.34, 20.26) * mm});
            skLineSegment(sketch, "E91.trimOffspring", {"start": v(14.68, 19.03) * mm, "end": v(14.26, 19.42) * mm});
            skLineSegment(sketch, "E92.trimOffspring", {"start": v(15.56, 18.22) * mm, "end": v(15.08, 18.67) * mm});
            skLineSegment(sketch, "E93.trimOffspring", {"start": v(16.41, 17.44) * mm, "end": v(15.96, 17.86) * mm});
            skLineSegment(sketch, "E94.trimOffspring", {"start": v(17.1, 16.82) * mm, "end": v(16.79, 17.1) * mm});
            skLineSegment(sketch, "E95.trimOffspring", {"start": v(17.94, 16.05) * mm, "end": v(17.55, 16.4) * mm});
            skLineSegment(sketch, "E96.trimOffspring", {"start": v(18.68, 15.37) * mm, "end": v(18.34, 15.68) * mm});
            skLineSegment(sketch, "E97.trimOffspring", {"start": v(19.43, 14.68) * mm, "end": v(19.07, 15) * mm});
            skLineSegment(sketch, "E98.trimOffspring", {"start": v(20.09, 14.08) * mm, "end": v(19.77, 14.37) * mm});
            skLineSegment(sketch, "E99", {"start": v(12.15, 22.42) * mm, "end": v(21.74, 13.63) * mm});
            skSolve(sketch);
        }
        {
            var Q0;
            Q0 = qSketchRegion(id + "F17", true);
            var Q1;
            {var subQ1=sQuery(id+"F0.wireOp",EDGE,"E5");var subQ5=sQuery(id+"F0.wireOp",EDGE,"E4");var subQ7=sQuery(id+"F0.wireOp",EDGE,"E0.left");var subQ8=makeQuery(id+"F1.opExtrude","SWEPT_FACE",FACE,{"disambiguationData":[OSD([subQ7])]});var subQ10=sQuery(id+"F0.wireOp",EDGE,"E0.right");var subQ13=sQuery(id+"F0.wireOp",EDGE,"E2");var subQ14=makeQuery(id+"F1.opExtrude","SWEPT_FACE",FACE,{"disambiguationData":[OSD([subQ13])]});var subQ16=sQuery(id+"F0.wireOp",EDGE,"E3");var subQ34=sQuery(id+"F0.wireOp",EDGE,"E6.bottom");var subQ35=sQuery(id+"F0.wireOp",EDGE,"E0.bottom");var subQ41=makeQuery(id+"F1.opExtrude","CAP_FACE",FACE,{"disambiguationData":[OSD([subQ35,subQ7,subQ10,subQ13,subQ16,subQ5,subQ1,subQ34])],"isStart":false});Q1=makeQuery(id+"F14.boolean.opBoolean","SPLIT",FACE,{"disambiguationData":[TD([subQ14])],"derivedFrom":makeQuery(id+"F6.boolean.opBoolean","SPLIT",FACE,{"disambiguationData":[TD([subQ8])],"derivedFrom":makeQuery(id+"F5.boolean.opBoolean","SPLIT",FACE,{"disambiguationData":[TD([subQ8])],"derivedFrom":subQ41})})});}
            var Q2;
            {var subQ1=sQuery(id+"F0.wireOp",EDGE,"E5");var subQ5=sQuery(id+"F0.wireOp",EDGE,"E4");var subQ7=sQuery(id+"F0.wireOp",EDGE,"E0.left");var subQ8=makeQuery(id+"F1.opExtrude","SWEPT_FACE",FACE,{"disambiguationData":[OSD([subQ7])]});var subQ10=sQuery(id+"F0.wireOp",EDGE,"E0.right");var subQ13=sQuery(id+"F0.wireOp",EDGE,"E2");var subQ14=makeQuery(id+"F1.opExtrude","SWEPT_FACE",FACE,{"disambiguationData":[OSD([subQ13])]});var subQ16=sQuery(id+"F0.wireOp",EDGE,"E3");var subQ34=sQuery(id+"F0.wireOp",EDGE,"E6.bottom");var subQ35=sQuery(id+"F0.wireOp",EDGE,"E0.bottom");var subQ41=makeQuery(id+"F1.opExtrude","CAP_FACE",FACE,{"disambiguationData":[OSD([subQ35,subQ7,subQ10,subQ13,subQ16,subQ5,subQ1,subQ34])],"isStart":false});Q2=makeQuery(id+"F14.boolean.opBoolean","SPLIT",FACE,{"disambiguationData":[TD([subQ14])],"derivedFrom":makeQuery(id+"F6.boolean.opBoolean","SPLIT",FACE,{"disambiguationData":[TD([subQ8])],"derivedFrom":makeQuery(id+"F5.boolean.opBoolean","SPLIT",FACE,{"disambiguationData":[TD([subQ8])],"derivedFrom":subQ41})})});}
            extrude(context, id + "F18", {"entities" : qUnion([Q0]), "operationType" : NewBodyOperationType.REMOVE, "endBound" : BoundingType.UP_TO_SURFACE, "endBoundEntityFace" : qUnion([Q1]), "depth" : 25 * mm});
        }
    });
